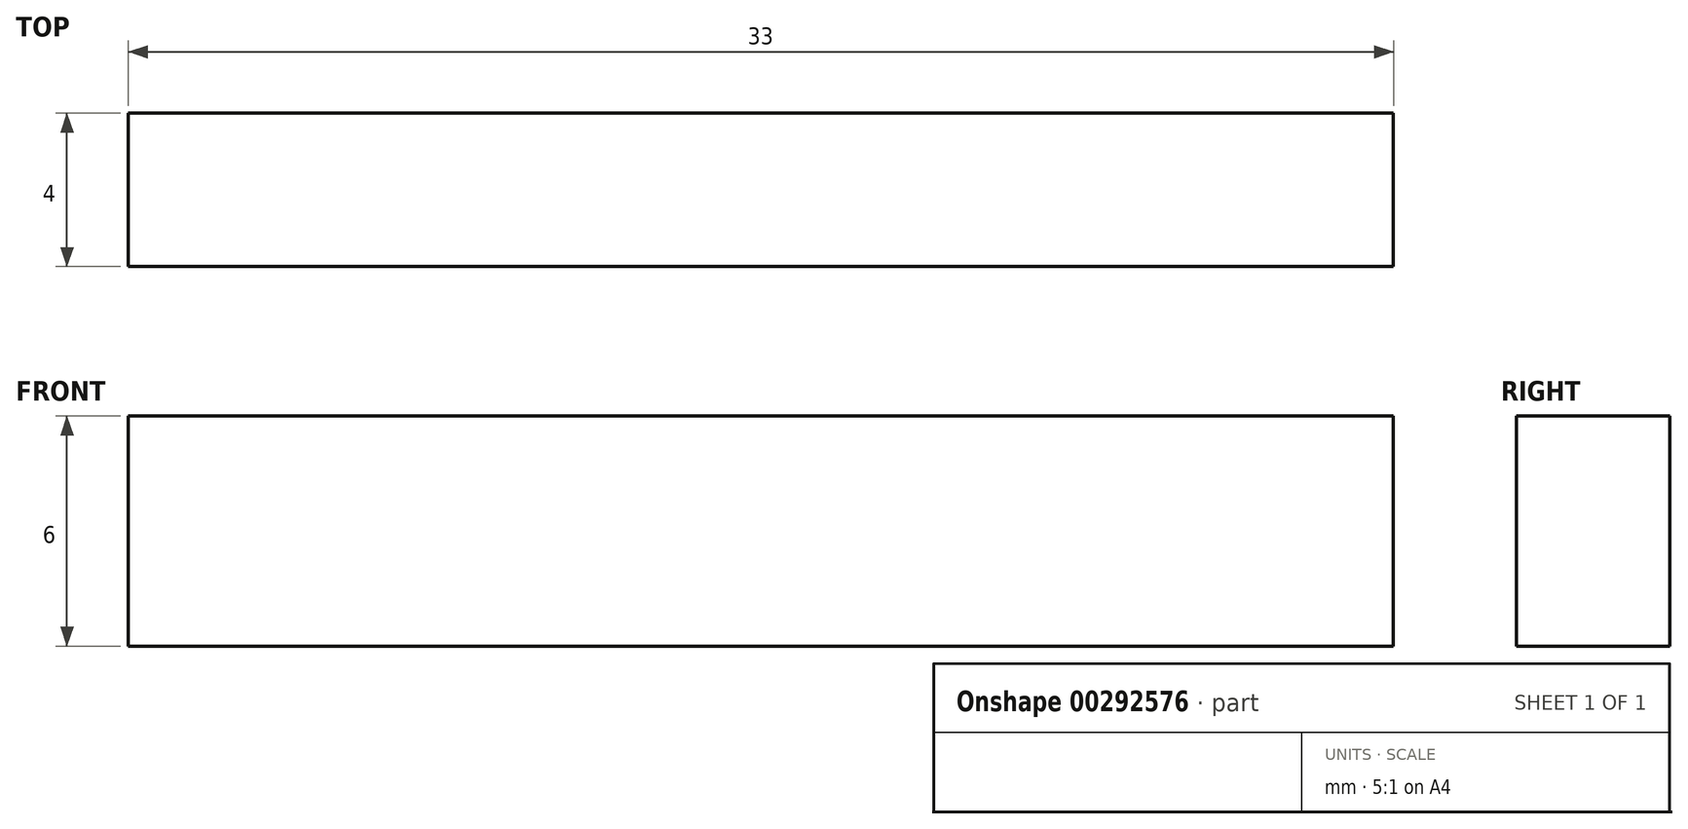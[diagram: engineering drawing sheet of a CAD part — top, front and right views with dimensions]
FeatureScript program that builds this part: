
annotation { "Feature Type Name" : "Feature", "Feature Type Description" : "" }
export const myFeature = defineFeature(function(context is Context, id is Id, definition is map)
    precondition{}
    {
        {
            var Q0;
            Q0=qCreatedBy(makeId("Front.planeOp"),FACE);
            var sketch = newSketch(context, id + "F0", { "sketchPlane" : qUnion([Q0])});
            skLineSegment(sketch, "E0", {"start": v(-17.55, -7.43) * mm, "end": v(15.45, -7.43) * mm});
            skLineSegment(sketch, "E1", {"start": v(15.45, -7.43) * mm, "end": v(15.45, -13.43) * mm});
            skLineSegment(sketch, "E2", {"start": v(15.45, -13.43) * mm, "end": v(-17.55, -13.43) * mm});
            skLineSegment(sketch, "E3", {"start": v(-17.55, -13.43) * mm, "end": v(-17.55, -7.43) * mm});
            skSolve(sketch);
        }
        {
            var Q0;
            Q0 = qSketchRegion(id + "F0", true);
            extrude(context, id + "F1", {"entities" : qUnion([Q0]), "depth" : 4 * mm});
        }
    });
